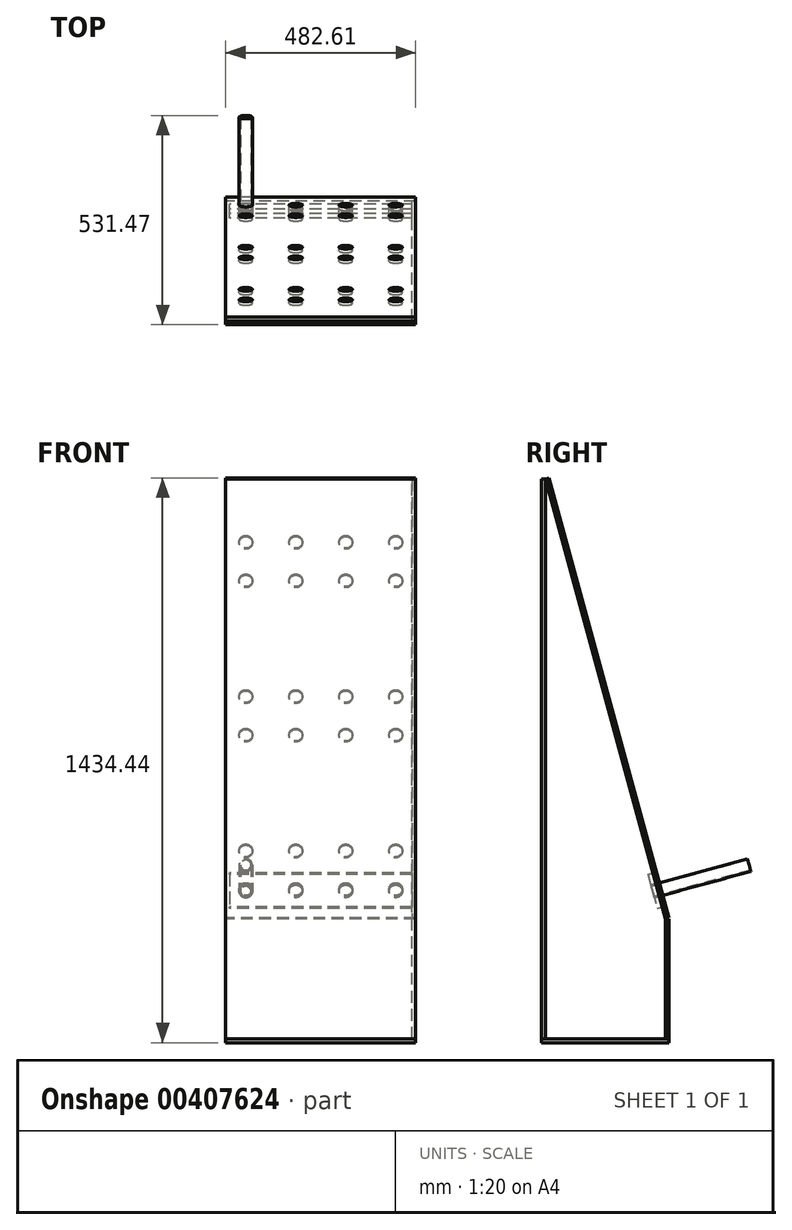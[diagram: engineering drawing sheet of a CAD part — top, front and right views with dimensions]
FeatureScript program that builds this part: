
annotation { "Feature Type Name" : "Feature", "Feature Type Description" : "" }
export const myFeature = defineFeature(function(context is Context, id is Id, definition is map)
    precondition{}
    {
        {
            var Q0;
            Q0=qCreatedBy(makeId("Right.planeOp"),FACE);
            var sketch = newSketch(context, id + "F0", { "sketchPlane" : qUnion([Q0])});
            skLineSegment(sketch, "E0.bottom", {"start": v(0, 0) * mm, "end": v(304.8, 0) * mm});
            skLineSegment(sketch, "E0.top", {"start": v(0, 1422.4) * mm, "end": v(0, 1422.4) * mm});
            skLineSegment(sketch, "E0.left", {"start": v(0, 0) * mm, "end": v(0, 1422.4) * mm});
            skLineSegment(sketch, "E0.right", {"start": v(304.8, 0) * mm, "end": v(304.8, 304.8) * mm});
            skLineSegment(sketch, "E1", {"start": v(0, 1422.4) * mm, "end": v(304.8, 304.8) * mm});
            skPoint(sketch, "E2.orphan", {"position": v(304.8, 1422.4) * mm});
            skSolve(sketch);
        }
        {
            var Q0;
            Q0=qSketchRegion(id+"F0",true);
            extrude(context, id + "F1", {"entities" : qUnion([Q0]), "depth" : 9.52 * mm});
        }
        {
            var Q0;
            Q0=makeQuery(id+"F1.opExtrude","SWEPT_FACE",FACE,{"disambiguationData":[OSD([sQuery(id+"F0.wireOp",EDGE,"E0.right")])]});
            var sketch = newSketch(context, id + "F2", { "sketchPlane" : qUnion([Q0])});
            skLineSegment(sketch, "E3.bottom", {"start": v(-9.53, 304.8) * mm, "end": v(473.08, 304.8) * mm});
            skLineSegment(sketch, "E3.top", {"start": v(-9.53, 0) * mm, "end": v(473.08, 0) * mm});
            skLineSegment(sketch, "E3.left", {"start": v(-9.53, 304.8) * mm, "end": v(-9.52, 0) * mm});
            skLineSegment(sketch, "E3.right", {"start": v(473.08, 304.8) * mm, "end": v(473.08, 0) * mm});
            skSolve(sketch);
        }
        {
            var Q0;
            Q0=qSketchRegion(id+"F2",true);
            extrude(context, id + "F3", {"entities" : qUnion([Q0]), "depth" : 9.52 * mm});
        }
        {
            var Q0;
            Q0=makeQuery(id+"F1.opExtrude","SWEPT_FACE",FACE,{"disambiguationData":[OSD([sQuery(id+"F0.wireOp",EDGE,"E1")])]});
            var sketch = newSketch(context, id + "F4", { "sketchPlane" : qUnion([Q0])});
            skLineSegment(sketch, "E4.bottom", {"start": v(-9.53, 1372.28) * mm, "end": v(473.08, 1372.28) * mm});
            skLineSegment(sketch, "E4.top", {"start": v(-9.53, 213.86) * mm, "end": v(473.08, 213.86) * mm});
            skLineSegment(sketch, "E4.left", {"start": v(-9.53, 1372.28) * mm, "end": v(-9.52, 213.86) * mm});
            skLineSegment(sketch, "E4.right", {"start": v(473.08, 1372.28) * mm, "end": v(473.08, 213.86) * mm});
            skSolve(sketch);
        }
        {
            var Q0;
            Q0=qSketchRegion(id+"F4",true);
            extrude(context, id + "F5", {"entities" : qUnion([Q0]), "depth" : 9.52 * mm});
        }
        {
            var Q0;
            Q0=makeQuery(id+"F1.opExtrude","SWEPT_FACE",FACE,{"disambiguationData":[OSD([sQuery(id+"F0.wireOp",EDGE,"E0.left")])]});
            var sketch = newSketch(context, id + "F6", { "sketchPlane" : qUnion([Q0])});
            skLineSegment(sketch, "E5.bottom", {"start": v(9.53, 0) * mm, "end": v(-473.08, 0) * mm});
            skLineSegment(sketch, "E5.top", {"start": v(9.52, 1422.4) * mm, "end": v(-473.08, 1422.4) * mm});
            skLineSegment(sketch, "E5.left", {"start": v(9.53, 0) * mm, "end": v(9.53, 1422.4) * mm});
            skLineSegment(sketch, "E5.right", {"start": v(-473.08, 0) * mm, "end": v(-473.08, 1422.4) * mm});
            skSolve(sketch);
        }
        {
            var Q0;
            Q0=qSketchRegion(id+"F6",true);
            extrude(context, id + "F7", {"entities" : qUnion([Q0]), "depth" : 9.52 * mm});
        }
        {
            var Q0;
            Q0=makeQuery(id+"F3.opExtrude","SWEPT_FACE",FACE,{"disambiguationData":[OSD([sQuery(id+"F2.wireOp",EDGE,"E3.top")])]});
            var sketch = newSketch(context, id + "F8", { "sketchPlane" : qUnion([Q0])});
            skLineSegment(sketch, "E6.bottom", {"start": v(-473.08, -314.33) * mm, "end": v(9.53, -314.33) * mm});
            skLineSegment(sketch, "E6.top", {"start": v(-473.08, 9.53) * mm, "end": v(9.52, 9.53) * mm});
            skLineSegment(sketch, "E6.left", {"start": v(-473.08, -314.33) * mm, "end": v(-473.08, 9.53) * mm});
            skLineSegment(sketch, "E6.right", {"start": v(9.53, -314.33) * mm, "end": v(9.52, 9.53) * mm});
            skSolve(sketch);
        }
        {
            var Q0;
            Q0=qSketchRegion(id+"F8",true);
            extrude(context, id + "F9", {"entities" : qUnion([Q0]), "depth" : 9.52 * mm});
        }
        {
            var Q0;
            Q0=makeQuery(id+"F5.opExtrude","CAP_FACE",FACE,{"disambiguationData":[OSD([sQuery(id+"F4.wireOp",EDGE,"E4.bottom"),sQuery(id+"F4.wireOp",EDGE,"E4.top"),sQuery(id+"F4.wireOp",EDGE,"E4.left"),sQuery(id+"F4.wireOp",EDGE,"E4.right")])],"isStart":false});
            var sketch = newSketch(context, id + "F10", { "sketchPlane" : qUnion([Q0])});
            skCircle(sketch, "E7", {"center": v(41.28, 290.06) * mm, "radius": 16.76 * mm});
            skCircle(sketch, "E8.0.1.0", {"center": v(41.28, 391.66) * mm, "radius": 16.76 * mm});
            skCircle(sketch, "E8.1.0.0", {"center": v(168.28, 290.06) * mm, "radius": 16.76 * mm});
            skCircle(sketch, "E8.1.1.0", {"center": v(168.28, 391.66) * mm, "radius": 16.76 * mm});
            skCircle(sketch, "E8.2.0.0", {"center": v(295.28, 290.06) * mm, "radius": 16.76 * mm});
            skCircle(sketch, "E8.2.1.0", {"center": v(295.28, 391.66) * mm, "radius": 16.76 * mm});
            skCircle(sketch, "E8.3.0.0", {"center": v(422.28, 290.06) * mm, "radius": 16.76 * mm});
            skCircle(sketch, "E8.3.1.0", {"center": v(422.28, 391.66) * mm, "radius": 16.76 * mm});
            skLineSegment(sketch, "E8.direction1", {"start": v(41.28, 290.06) * mm, "end": v(168.28, 290.06) * mm, "construction": true});
            skLineSegment(sketch, "E8.direction2", {"start": v(41.28, 290.06) * mm, "end": v(41.28, 391.66) * mm, "construction": true});
            skCircle(sketch, "E9.0.1.0", {"center": v(422.28, 696.46) * mm, "radius": 16.76 * mm});
            skCircle(sketch, "E9.0.1.1", {"center": v(422.28, 798.06) * mm, "radius": 16.76 * mm});
            skLineSegment(sketch, "E9.0.1.2", {"start": v(41.28, 696.46) * mm, "end": v(41.28, 798.06) * mm, "construction": true});
            skCircle(sketch, "E9.0.1.3", {"center": v(168.28, 696.46) * mm, "radius": 16.76 * mm});
            skCircle(sketch, "E9.0.1.4", {"center": v(168.28, 798.06) * mm, "radius": 16.76 * mm});
            skCircle(sketch, "E9.0.1.5", {"center": v(295.28, 696.46) * mm, "radius": 16.76 * mm});
            skCircle(sketch, "E9.0.1.6", {"center": v(41.28, 798.06) * mm, "radius": 16.76 * mm});
            skCircle(sketch, "E9.0.1.7", {"center": v(41.28, 696.46) * mm, "radius": 16.76 * mm});
            skLineSegment(sketch, "E9.0.1.8", {"start": v(41.28, 696.46) * mm, "end": v(168.28, 696.46) * mm, "construction": true});
            skCircle(sketch, "E9.0.1.9", {"center": v(295.28, 798.06) * mm, "radius": 16.76 * mm});
            skCircle(sketch, "E9.0.2.0", {"center": v(422.28, 1102.86) * mm, "radius": 16.76 * mm});
            skCircle(sketch, "E9.0.2.1", {"center": v(422.28, 1204.46) * mm, "radius": 16.76 * mm});
            skLineSegment(sketch, "E9.0.2.2", {"start": v(41.28, 1102.86) * mm, "end": v(41.28, 1204.46) * mm, "construction": true});
            skCircle(sketch, "E9.0.2.3", {"center": v(168.28, 1102.86) * mm, "radius": 16.76 * mm});
            skCircle(sketch, "E9.0.2.4", {"center": v(168.28, 1204.46) * mm, "radius": 16.76 * mm});
            skCircle(sketch, "E9.0.2.5", {"center": v(295.28, 1102.86) * mm, "radius": 16.76 * mm});
            skCircle(sketch, "E9.0.2.6", {"center": v(41.28, 1204.46) * mm, "radius": 16.76 * mm});
            skCircle(sketch, "E9.0.2.7", {"center": v(41.28, 1102.86) * mm, "radius": 16.76 * mm});
            skLineSegment(sketch, "E9.0.2.8", {"start": v(41.28, 1102.86) * mm, "end": v(168.28, 1102.86) * mm, "construction": true});
            skCircle(sketch, "E9.0.2.9", {"center": v(295.28, 1204.46) * mm, "radius": 16.76 * mm});
            skCircle(sketch, "E9.0.3.0", {"center": v(422.28, 1509.26) * mm, "radius": 16.76 * mm});
            skCircle(sketch, "E9.0.3.1", {"center": v(422.28, 1610.86) * mm, "radius": 16.76 * mm});
            skLineSegment(sketch, "E9.0.3.2", {"start": v(41.28, 1509.26) * mm, "end": v(41.28, 1610.86) * mm, "construction": true});
            skCircle(sketch, "E9.0.3.3", {"center": v(168.28, 1509.26) * mm, "radius": 16.76 * mm});
            skCircle(sketch, "E9.0.3.4", {"center": v(168.28, 1610.86) * mm, "radius": 16.76 * mm});
            skCircle(sketch, "E9.0.3.5", {"center": v(295.28, 1509.26) * mm, "radius": 16.76 * mm});
            skCircle(sketch, "E9.0.3.6", {"center": v(41.28, 1610.86) * mm, "radius": 16.76 * mm});
            skCircle(sketch, "E9.0.3.7", {"center": v(41.28, 1509.26) * mm, "radius": 16.76 * mm});
            skLineSegment(sketch, "E9.0.3.8", {"start": v(41.28, 1509.26) * mm, "end": v(168.28, 1509.26) * mm, "construction": true});
            skCircle(sketch, "E9.0.3.9", {"center": v(295.28, 1610.86) * mm, "radius": 16.76 * mm});
            skLineSegment(sketch, "E9.direction1", {"start": v(41.28, 290.06) * mm, "end": v(620.4, 290.06) * mm, "construction": true});
            skLineSegment(sketch, "E9.direction2", {"start": v(41.28, 290.06) * mm, "end": v(41.28, 696.46) * mm, "construction": true});
            skSolve(sketch);
        }
        {
            var Q0;
            Q0=qSketchRegion(id+"F10",true);
            extrude(context, id + "F11", {"entities" : qUnion([Q0]), "operationType" : NewBodyOperationType.REMOVE, "oppositeDirection" : true, "depth" : 12.7 * mm});
        }
        {
            var Q0;
            Q0=makeQuery(id+"F5.opExtrude","CAP_FACE",FACE,{"disambiguationData":[OSD([sQuery(id+"F4.wireOp",EDGE,"E4.bottom"),sQuery(id+"F4.wireOp",EDGE,"E4.top"),sQuery(id+"F4.wireOp",EDGE,"E4.left"),sQuery(id+"F4.wireOp",EDGE,"E4.right")])],"isStart":true});
            var sketch = newSketch(context, id + "F12", { "sketchPlane" : qUnion([Q0])});
            skLineSegment(sketch, "E10.bottom", {"start": v(0, 334.51) * mm, "end": v(-463.55, 334.51) * mm});
            skLineSegment(sketch, "E10.top", {"start": v(0, 245.61) * mm, "end": v(-463.55, 245.61) * mm});
            skLineSegment(sketch, "E10.left", {"start": v(0, 334.51) * mm, "end": v(0, 245.61) * mm});
            skLineSegment(sketch, "E10.right", {"start": v(-463.55, 334.51) * mm, "end": v(-463.55, 245.61) * mm});
            skCircle(sketch, "E11", {"center": v(-41.28, 290.06) * mm, "radius": 16.76 * mm});
            skCircle(sketch, "E12", {"center": v(-168.28, 290.06) * mm, "radius": 16.76 * mm});
            skCircle(sketch, "E13", {"center": v(-295.28, 290.06) * mm, "radius": 16.76 * mm});
            skCircle(sketch, "E14", {"center": v(-422.28, 290.06) * mm, "radius": 16.76 * mm});
            skSolve(sketch);
        }
        {
            var Q0;
            Q0=qSketchRegion(id+"F12",true);
            extrude(context, id + "F13", {"entities" : qUnion([Q0]), "depth" : 12.7 * mm});
        }
        {
            var Q0;
            Q0=makeQuery(id+"F13.opExtrude","CAP_FACE",FACE,{"disambiguationData":[OSD([sQuery(id+"F12.wireOp",EDGE,"E10.bottom"),sQuery(id+"F12.wireOp",EDGE,"E10.top"),sQuery(id+"F12.wireOp",EDGE,"E10.left"),sQuery(id+"F12.wireOp",EDGE,"E10.right"),sQuery(id+"F12.wireOp",EDGE,"E11"),sQuery(id+"F12.wireOp",EDGE,"E12"),sQuery(id+"F12.wireOp",EDGE,"E13"),sQuery(id+"F12.wireOp",EDGE,"E14")])],"isStart":false});
            var sketch = newSketch(context, id + "F14", { "sketchPlane" : qUnion([Q0])});
            skCircle(sketch, "E15", {"center": v(-422.28, 290.06) * mm, "radius": 16.7 * mm});
            skCircle(sketch, "E16", {"center": v(-422.28, 290.06) * mm, "radius": 13.34 * mm});
            skSolve(sketch);
        }
        {
            var Q0;
            Q0=qSketchRegion(id+"F14",true);
            extrude(context, id + "F15", {"entities" : qUnion([Q0]), "oppositeDirection" : true, "depth" : 254 * mm});
        }
    });
